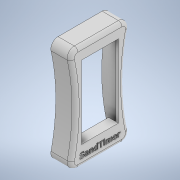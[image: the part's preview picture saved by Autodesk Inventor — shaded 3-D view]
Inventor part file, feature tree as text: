
AUTODESK INVENTOR PART (.ipt)
format: ipt  version: 2021 (Build 250183000, 183)  size: 542,208 bytes
history: native  units: mm
features: extrude x7, sketch x7, fillet x3, mirror x2, shell x1, plane x1, thicken_offset x1, projected_geometry x1
ambient origin geometry x8: Origin, YZ Plane, XZ Plane, XY Plane, X Axis, Y Axis, Z Axis, Center Point
bodies: Solid1 (feature_tree)
feature tree (23):
  extrude  "Extrusion1"  Depth=27.0mm
  extrude  "Extrusion5"  Depth=2.0mm
  fillet  "Fillet1"  Radius=1.5mm
  shell  "Shell1"  Thickness=3.8mm
  extrude  "Extrusion9"  Depth=4.0mm
  extrude  "Extrusion12"  Depth=41.0mm
  extrude  "Extrusion17"  TaperAngle=0.0deg  [1 undecoded]
  fillet  "Fillet13"  Radius=24.0mm
  extrude  "Extrusion18"  Depth=4.0mm
  mirror  "Mirror9"
  plane  "Work Plane8"
  mirror  "Mirror10"
  thicken_offset  "Thicken1"
  extrude  "Extrusion19"  Depth=1.0mm
  fillet  "Fillet14"  Radius=1.9mm
  sketch  "Sketch1"  dims[d0=11.0mm d1=27.0mm]
  sketch  "Sketch5"  dims[d2=58.0mm d3=0.0mm d4=2.0mm d5=1.5mm d26=3.8mm]
  sketch  "Sketch9"  dims[d27=0.0mm d28=0.0mm d29=4.0mm]
  sketch  "Sketch12"  dims[d53=21.0mm d54=41.0mm]
  sketch  "Sketch17"  dims[d55=6.54mm d56=0.0mm d57=0.0mm d68=24.0mm]
  sketch  "Sketch18"  dims[d69=4.0mm d70=3.0mm]
  sketch  "Sketch19"  dims[d71=0.5mm d72=0.0mm d99=1.0mm d106=1.9mm d107=4.0mm d110=4.0mm d111=0.0mm d112=0.5mm d113=4.0mm d114=0.0mm d115=1.5mm d116=0.25mm d117=0.25mm d118=1.5mm d119=1.5mm d120=4.0mm d121=0.0mm d122=0.5mm]
  projected_geometry  "Project Cut Edges12"
note: 1 required parameter value undecoded (feature->parameter linkage not recoverable at this tier; creation-order binding heuristic only, values carry confidence <= 0.55)
